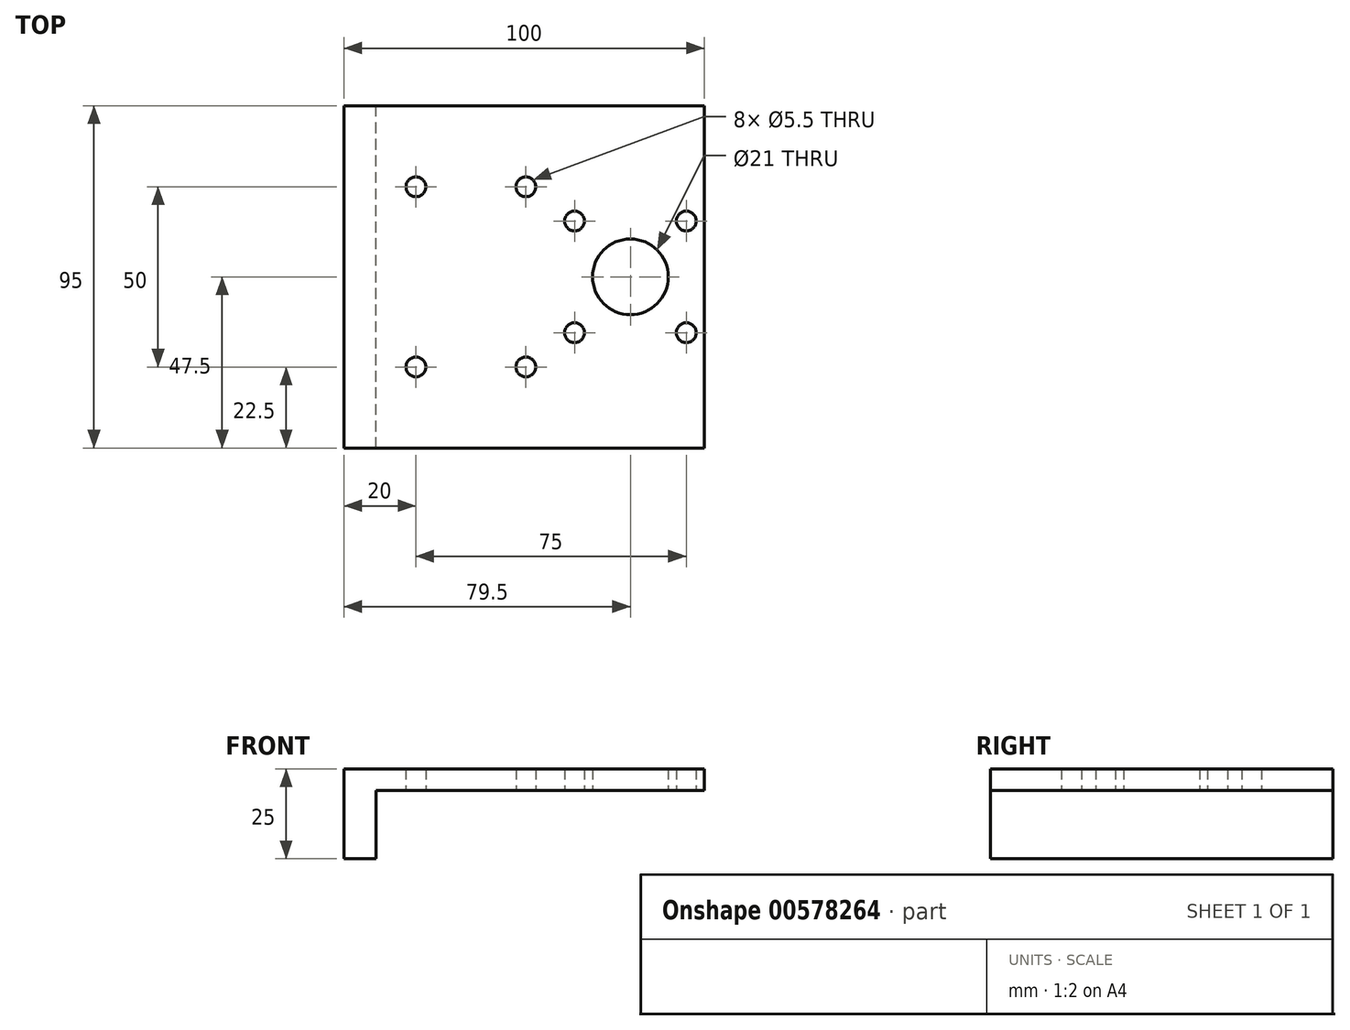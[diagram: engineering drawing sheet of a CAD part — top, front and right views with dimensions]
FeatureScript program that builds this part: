
annotation { "Feature Type Name" : "Feature", "Feature Type Description" : "" }
export const myFeature = defineFeature(function(context is Context, id is Id, definition is map)
    precondition{}
    {
        {
            var Q0;
            Q0=qCreatedBy(makeId("Front.planeOp"),FACE);
            var sketch = newSketch(context, id + "F0", { "sketchPlane" : qUnion([Q0])});
            skLineSegment(sketch, "E0", {"start": v(0, 0) * mm, "end": v(-100, 0) * mm});
            skLineSegment(sketch, "E1", {"start": v(-100, 0) * mm, "end": v(-100, -25) * mm});
            skLineSegment(sketch, "E2", {"start": v(-100, -25) * mm, "end": v(-91, -25) * mm});
            skLineSegment(sketch, "E3", {"start": v(-91, -25) * mm, "end": v(-91, -6) * mm});
            skLineSegment(sketch, "E4", {"start": v(-91, -6) * mm, "end": v(0, -6) * mm});
            skLineSegment(sketch, "E5", {"start": v(0, -6) * mm, "end": v(0, 0) * mm});
            skSolve(sketch);
        }
        {
            var Q0;
            Q0 = qSketchRegion(id + "F0", true);
            extrude(context, id + "F1", {"entities" : qUnion([Q0]), "depth" : 95 * mm, "offsetDistance" : 25 * mm});
        }
        {
            var Q0;
            Q0=makeQuery(id+"F1.opExtrude","SWEPT_FACE",FACE,{"disambiguationData":[OSD([sQuery(id+"F0.wireOp",EDGE,"E4")])]});
            var sketch = newSketch(context, id + "F2", { "sketchPlane" : qUnion([Q0])});
            skCircle(sketch, "E6", {"center": v(-80, 72.5) * mm, "radius": 2.75 * mm});
            skCircle(sketch, "E7", {"center": v(-49.5, 72.5) * mm, "radius": 2.75 * mm});
            skCircle(sketch, "E8", {"center": v(-80, 22.5) * mm, "radius": 2.75 * mm});
            skCircle(sketch, "E9", {"center": v(-49.5, 22.5) * mm, "radius": 2.75 * mm});
            skCircle(sketch, "E10", {"center": v(-5, 32) * mm, "radius": 2.75 * mm});
            skCircle(sketch, "E11", {"center": v(-5, 63) * mm, "radius": 2.75 * mm});
            skCircle(sketch, "E12", {"center": v(-36, 32) * mm, "radius": 2.75 * mm});
            skCircle(sketch, "E13", {"center": v(-36, 63) * mm, "radius": 2.75 * mm});
            skCircle(sketch, "E14", {"center": v(-20.5, 47.5) * mm, "radius": 10.5 * mm});
            skLineSegment(sketch, "E15", {"start": v(-5, 32) * mm, "end": v(-36, 63) * mm, "construction": true});
            skLineSegment(sketch, "E16", {"start": v(-36, 32) * mm, "end": v(-5, 63) * mm, "construction": true});
            skLineSegment(sketch, "E17", {"start": v(-42, 66.95) * mm, "end": v(-42, 36.97) * mm, "construction": true});
            skSolve(sketch);
        }
        {
            var Q0;
            Q0 = qSketchRegion(id + "F2", true);
            extrude(context, id + "F3", {"entities" : qUnion([Q0]), "operationType" : NewBodyOperationType.REMOVE, "oppositeDirection" : true, "depth" : 6 * mm, "offsetDistance" : 25 * mm});
        }
    });
